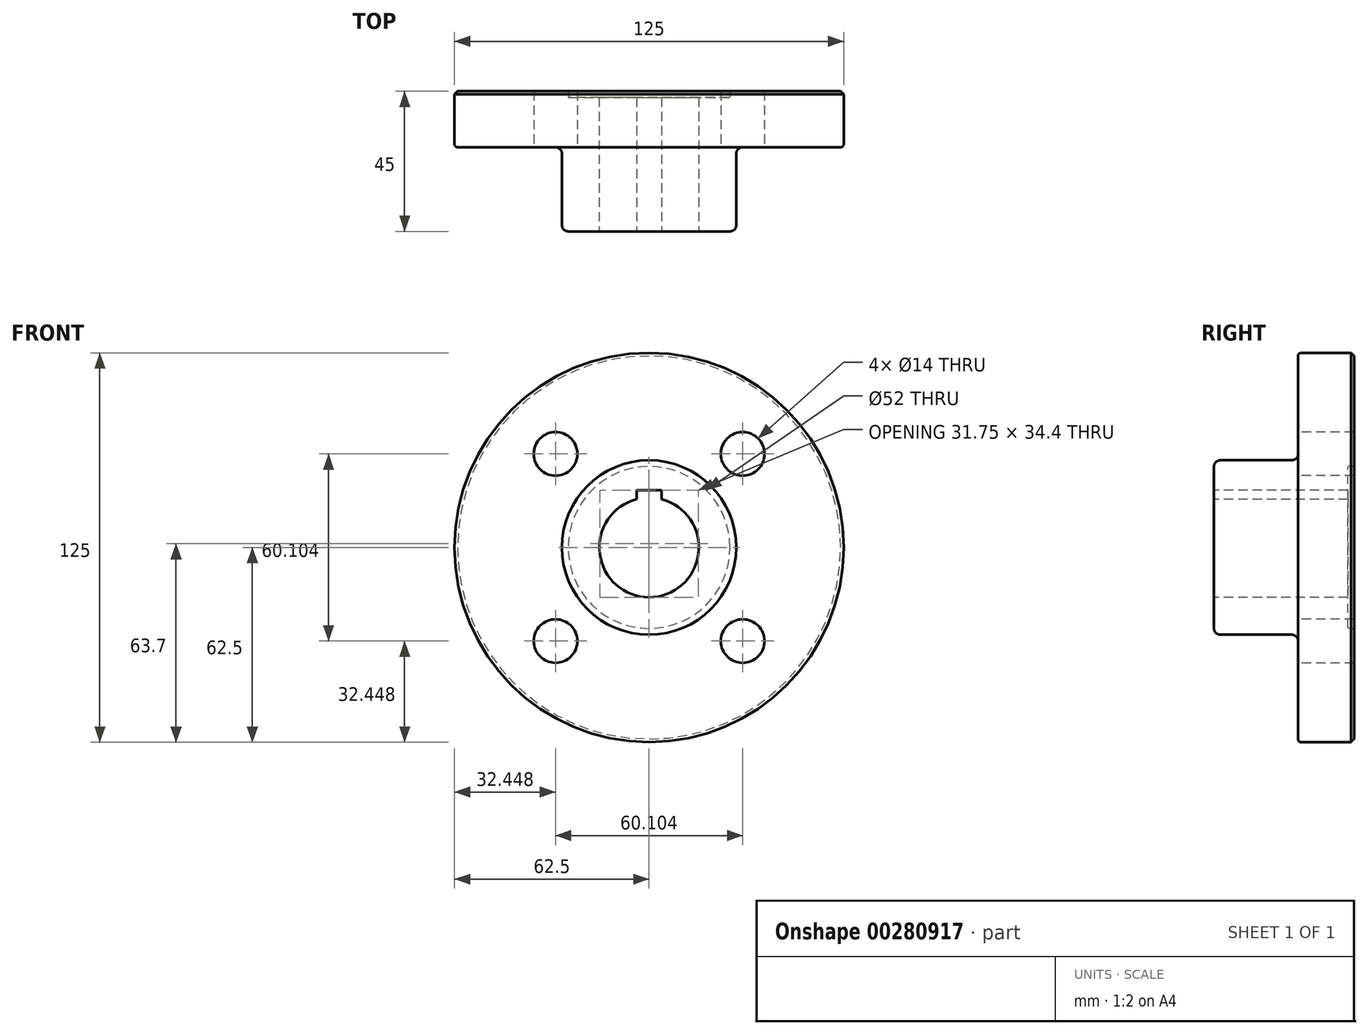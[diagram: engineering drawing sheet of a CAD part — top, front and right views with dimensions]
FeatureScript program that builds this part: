
annotation { "Feature Type Name" : "Feature", "Feature Type Description" : "" }
export const myFeature = defineFeature(function(context is Context, id is Id, definition is map)
    precondition{}
    {
        {
            var Q0;
            Q0=qCreatedBy(makeId("Right.planeOp"),FACE);
            var sketch = newSketch(context, id + "F0", { "sketchPlane" : qUnion([Q0])});
            skLineSegment(sketch, "E0", {"start": v(0, 26) * mm, "end": v(0, 62.5) * mm});
            skLineSegment(sketch, "E1", {"start": v(0, 62.5) * mm, "end": v(-18, 62.5) * mm});
            skLineSegment(sketch, "E2", {"start": v(-18, 62.5) * mm, "end": v(-18, 28) * mm});
            skLineSegment(sketch, "E3", {"start": v(-18, 28) * mm, "end": v(-45, 28) * mm});
            skLineSegment(sketch, "E4", {"start": v(-45, 28) * mm, "end": v(-45, 16) * mm});
            skLineSegment(sketch, "E5", {"start": v(-45, 16) * mm, "end": v(-2, 16) * mm});
            skLineSegment(sketch, "E6", {"start": v(-2, 16) * mm, "end": v(-2, 26) * mm});
            skLineSegment(sketch, "E7", {"start": v(-2, 26) * mm, "end": v(0, 26) * mm});
            skPoint(sketch, "E8.orphan", {"position": v(0, 16) * mm});
            skLineSegment(sketch, "E9", {"start": v(-59.2, 0) * mm, "end": v(14.4, 0) * mm, "construction": true});
            skSolve(sketch);
        }
        {
            var Q0;
            Q0=makeQuery(id+"F0.imprint","IMPRINT",FACE,{"disambiguationData":[TD([[makeQuery(id+"F0.imprint","IMPRINT",EDGE,{"derivedFrom":sQuery(id+"F0.wireOp",EDGE,"E0")}),1.0]])]});
            var Q1;
            Q1=sQuery(id+"F0.wireOp",EDGE,"E9");
            revolve(context, id + "F1", {"entities" : qUnion([Q0]), "axis" : qUnion([Q1]), "revolveType" : RevolveType.FULL});
        }
        {
            var Q0;
            Q0=makeQuery(id+"F1.opRevolve","SWEPT_FACE",FACE,{"disambiguationData":[OSD([sQuery(id+"F0.wireOp",EDGE,"E4")])]});
            var sketch = newSketch(context, id + "F2", { "sketchPlane" : qUnion([Q0])});
            skLineSegment(sketch, "E10.bottom", {"start": v(-4, 18.4) * mm, "end": v(4, 18.4) * mm});
            skLineSegment(sketch, "E10.top", {"start": v(-4, 12) * mm, "end": v(4, 12) * mm});
            skLineSegment(sketch, "E10.left", {"start": v(-4, 18.4) * mm, "end": v(-4, 12) * mm});
            skLineSegment(sketch, "E10.right", {"start": v(4, 18.4) * mm, "end": v(4, 12) * mm});
            skSolve(sketch);
        }
        {
            var Q0;
            {var subQ0=sQuery(id+"F2.wireOp",EDGE,"E10.top");Q0=makeQuery(id+"F2.imprint","IMPRINT",FACE,{"disambiguationData":[TD([[makeQuery(id+"F2.imprint","IMPRINT",EDGE,{"derivedFrom":subQ0}),1.0]])]});}
            var Q1;
            {var subQ0=sQuery(id+"F2.wireOp",EDGE,"E10.bottom");Q1=makeQuery(id+"F2.imprint","IMPRINT",FACE,{"disambiguationData":[TD([[makeQuery(id+"F2.imprint","IMPRINT",EDGE,{"derivedFrom":subQ0}),-1.0]])]});}
            extrude(context, id + "F3", {"entities" : qUnion([Q0, Q1]), "operationType" : NewBodyOperationType.REMOVE, "endBound" : BoundingType.THROUGH_ALL, "oppositeDirection" : true, "depth" : 25 * mm});
        }
        {
            var Q0;
            Q0=makeQuery(id+"F1.opRevolve","SWEPT_FACE",FACE,{"disambiguationData":[OSD([sQuery(id+"F0.wireOp",EDGE,"E2")])]});
            var sketch = newSketch(context, id + "F4", { "sketchPlane" : qUnion([Q0])});
            skLineSegment(sketch, "E11", {"start": v(0, 0) * mm, "end": v(30.05, 30.05) * mm, "construction": true});
            skLineSegment(sketch, "E12.MirrorCS", {"start": v(0, 0) * mm, "end": v(30.05, -30.05) * mm, "construction": true});
            skLineSegment(sketch, "E13.MirrorCS", {"start": v(0, 0) * mm, "end": v(-30.05, 30.05) * mm, "construction": true});
            skLineSegment(sketch, "E14.MirrorCS", {"start": v(0, 0) * mm, "end": v(-30.05, -30.05) * mm, "construction": true});
            skSolve(sketch);
        }
        {
            var Q0;
            Q0=sQuery(id+"F4.wireOp",VERTEX,"E11.end");
            var Q1;
            Q1=sQuery(id+"F4.wireOp",VERTEX,"E12.MirrorCS.end");
            var Q2;
            Q2=sQuery(id+"F4.wireOp",VERTEX,"E14.MirrorCS.end");
            var Q3;
            Q3=sQuery(id+"F4.wireOp",VERTEX,"E13.MirrorCS.end");
            var Q4;
            Q4=makeQuery(id+"F1.opRevolve","SWEPT_BODY",BODY,{"disambiguationData":[OSD([sQuery(id+"F0.wireOp",EDGE,"E0"),sQuery(id+"F0.wireOp",EDGE,"E1"),sQuery(id+"F0.wireOp",EDGE,"E2"),sQuery(id+"F0.wireOp",EDGE,"E3"),sQuery(id+"F0.wireOp",EDGE,"E4"),sQuery(id+"F0.wireOp",EDGE,"E5"),sQuery(id+"F0.wireOp",EDGE,"E6"),sQuery(id+"F0.wireOp",EDGE,"E7")])]});
            hole(context, id + "F5", {"style" : HoleStyle.SIMPLE, "endStyle" : HoleEndStyle.THROUGH, "holeDiameter" : 14 * mm, "tappedDepth" : 12 * mm, "tapClearance" : 3, "locations" : qUnion([Q0, Q1, Q2, Q3]), "scope" : qUnion([Q4])});
        }
        {
            var Q0;
            Q0=makeQuery(id+"F1.opRevolve","SWEPT_EDGE",EDGE,{"disambiguationData":[OSD([sQuery(id+"F0.wireOp",EDGE,"E2"),sQuery(id+"F0.wireOp",EDGE,"E3")])]});
            var Q1;
            Q1=makeQuery(id+"F1.opRevolve","SWEPT_EDGE",EDGE,{"disambiguationData":[OSD([sQuery(id+"F0.wireOp",EDGE,"E3"),sQuery(id+"F0.wireOp",EDGE,"E4")])]});
            fillet(context, id + "F6", {"entities" : qUnion([Q0, Q1]), "radius" : 2 * mm, "tangentPropagation" : true, "allowEdgeOverflow" : false});
        }
        {
            var Q0;
            Q0=makeQuery(id+"F1.opRevolve","SWEPT_EDGE",EDGE,{"disambiguationData":[OSD([sQuery(id+"F0.wireOp",EDGE,"E1"),sQuery(id+"F0.wireOp",EDGE,"E2")])]});
            fillet(context, id + "F7", {"entities" : qUnion([Q0]), "radius" : 1 * mm, "tangentPropagation" : true, "allowEdgeOverflow" : false});
        }
        {
            var Q0;
            Q0=makeQuery(id+"F1.opRevolve","SWEPT_EDGE",EDGE,{"disambiguationData":[OSD([sQuery(id+"F0.wireOp",EDGE,"E0"),sQuery(id+"F0.wireOp",EDGE,"E1")])]});
            chamfer(context, id + "F8", {"entities" : qUnion([Q0]), "width" : 1 * mm, "tangentPropagation" : true});
        }
        {
            var Q0;
            Q0=makeQuery(id+"F1.opRevolve","SWEPT_EDGE",EDGE,{"disambiguationData":[OSD([sQuery(id+"F0.wireOp",EDGE,"E0"),sQuery(id+"F0.wireOp",EDGE,"E7")])]});
            fillet(context, id + "F9", {"entities" : qUnion([Q0]), "radius" : 0.5 * mm, "tangentPropagation" : true, "allowEdgeOverflow" : false});
        }
        {
            var Q0;
            Q0=makeQuery(id+"F1.opRevolve","SWEPT_EDGE",EDGE,{"disambiguationData":[OSD([sQuery(id+"F0.wireOp",EDGE,"E6"),sQuery(id+"F0.wireOp",EDGE,"E7")])]});
            fillet(context, id + "F10", {"entities" : qUnion([Q0]), "radius" : 0.4 * mm, "tangentPropagation" : true, "allowEdgeOverflow" : false});
        }
    });
